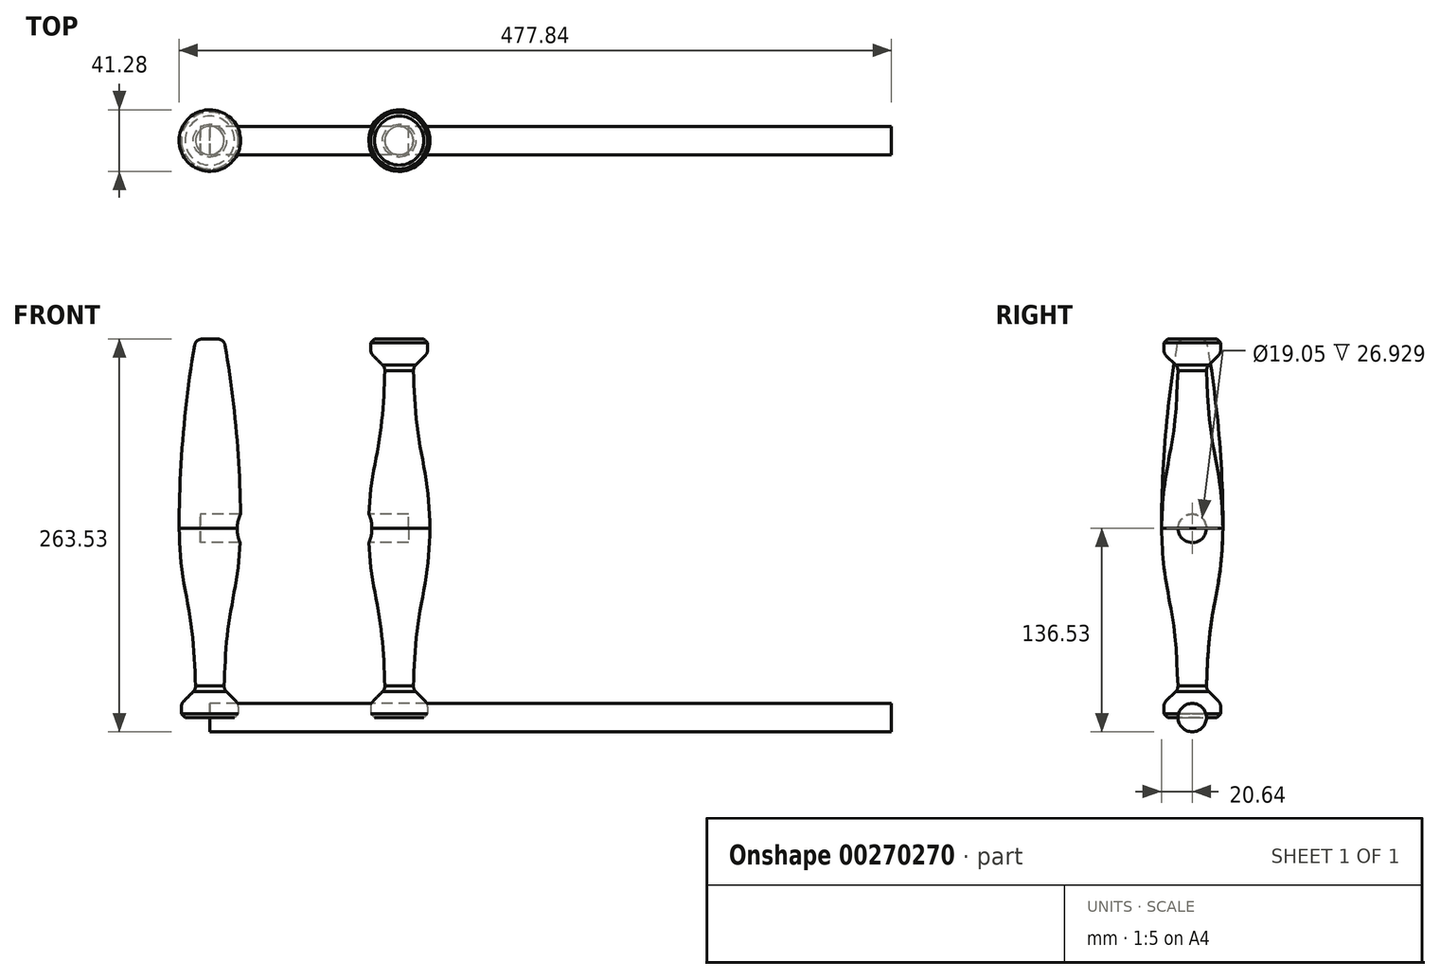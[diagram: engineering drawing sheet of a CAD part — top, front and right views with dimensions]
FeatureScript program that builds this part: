
annotation { "Feature Type Name" : "Feature", "Feature Type Description" : "" }
export const myFeature = defineFeature(function(context is Context, id is Id, definition is map)
    precondition{}
    {
        {
            var Q0;
            Q0=qCreatedBy(makeId("Top.planeOp"),FACE);
            var sketch = newSketch(context, id + "F0", { "sketchPlane" : qUnion([Q0])});
            skCircle(sketch, "E0", {"center": v(0, 0) * mm, "radius": 19.05 * mm});
            skSolve(sketch);
        }
        {
            var Q0;
            Q0=makeQuery(id+"F0.imprint","IMPRINT",FACE,{"disambiguationData":[TD([[makeQuery(id+"F0.imprint","IMPRINT",EDGE,{"derivedFrom":sQuery(id+"F0.wireOp",EDGE,"E0")}),1.0]])]});
            extrude(context, id + "F1", {"entities" : qUnion([Q0]), "depth" : 9.52 * mm});
        }
        {
            var Q0;
            Q0=qCreatedBy(makeId("Top.planeOp"),FACE);
            cPlane(context, id + "F2", {"entities" : qUnion([Q0]), "cplaneType" : CPlaneType.OFFSET, "offset" : 19.05 * mm, "width" : 152.4 * mm, "height" : 152.4 * mm});
        }
        {
            var Q0;
            Q0=qCreatedBy(id+"F2.planeOp",FACE);
            var sketch = newSketch(context, id + "F3", { "sketchPlane" : qUnion([Q0])});
            skCircle(sketch, "E1", {"center": v(0, 0) * mm, "radius": 9.53 * mm});
            skSolve(sketch);
        }
        {
            var Q0;
            Q0=qCreatedBy(makeId("Top.planeOp"),FACE);
            cPlane(context, id + "F4", {"entities" : qUnion([Q0]), "cplaneType" : CPlaneType.OFFSET, "offset" : 127 * mm, "width" : 152.4 * mm, "height" : 152.4 * mm});
        }
        {
            var Q0;
            Q0=qCreatedBy(id+"F4.planeOp",FACE);
            var sketch = newSketch(context, id + "F5", { "sketchPlane" : qUnion([Q0])});
            skCircle(sketch, "E2", {"center": v(0, 0) * mm, "radius": 20.64 * mm});
            skSolve(sketch);
        }
        {
            var Q0;
            Q0=qCreatedBy(makeId("Top.planeOp"),FACE);
            cPlane(context, id + "F6", {"entities" : qUnion([Q0]), "cplaneType" : CPlaneType.OFFSET, "offset" : 63.5 * mm, "width" : 152.4 * mm, "height" : 152.4 * mm});
        }
        {
            var Q0;
            Q0=qCreatedBy(id+"F6.planeOp",FACE);
            var sketch = newSketch(context, id + "F7", { "sketchPlane" : qUnion([Q0])});
            skCircle(sketch, "E3", {"center": v(0, 0) * mm, "radius": 12.7 * mm});
            skSolve(sketch);
        }
        {
            var Q0;
            Q0=qCreatedBy(makeId("Top.planeOp"),FACE);
            cPlane(context, id + "F8", {"entities" : qUnion([Q0]), "cplaneType" : CPlaneType.OFFSET, "offset" : 101.6 * mm, "width" : 152.4 * mm, "height" : 152.4 * mm});
        }
        {
            var Q0;
            Q0=qCreatedBy(id+"F8.planeOp",FACE);
            var sketch = newSketch(context, id + "F9", { "sketchPlane" : qUnion([Q0])});
            skCircle(sketch, "E4", {"center": v(0, 0) * mm, "radius": 19.05 * mm});
            skSolve(sketch);
        }
        {
            var Q1;
            Q1=makeQuery(id+"F1.opExtrude","CAP_FACE",FACE,{"disambiguationData":[OSD([sQuery(id+"F0.wireOp",EDGE,"E0")])],"isStart":false});
            var Q2;
            Q2=makeQuery(id+"F3.imprint","IMPRINT",FACE,{"disambiguationData":[TD([[makeQuery(id+"F3.imprint","IMPRINT",EDGE,{"derivedFrom":sQuery(id+"F3.wireOp",EDGE,"E1")}),1.0]])]});
            loft(context, id + "F10", {"operationType" : NewBodyOperationType.ADD, "sheetProfilesArray" : [{ "sheetProfileEntities" : qUnion([Q1]) }, { "sheetProfileEntities" : qUnion([Q2]) }]});
        }
        {
            var Q1;
            Q1=makeQuery(id+"F10.opLoft","CAP_FACE",FACE,{"disambiguationData":[OSD([makeQuery(id+"F3.imprint","IMPRINT",FACE,{"disambiguationData":[TD([[makeQuery(id+"F3.imprint","IMPRINT",EDGE,{"derivedFrom":sQuery(id+"F3.wireOp",EDGE,"E1")}),1.0]])]})])],"isStart":true});
            var Q2;
            Q2=makeQuery(id+"F7.imprint","IMPRINT",FACE,{"disambiguationData":[TD([[makeQuery(id+"F7.imprint","IMPRINT",EDGE,{"derivedFrom":sQuery(id+"F7.wireOp",EDGE,"E3")}),1.0]])]});
            var Q3;
            Q3=makeQuery(id+"F9.imprint","IMPRINT",FACE,{"disambiguationData":[TD([[makeQuery(id+"F9.imprint","IMPRINT",EDGE,{"derivedFrom":sQuery(id+"F9.wireOp",EDGE,"E4")}),1.0]])]});
            var Q4;
            Q4=makeQuery(id+"F5.imprint","IMPRINT",FACE,{"disambiguationData":[TD([[makeQuery(id+"F5.imprint","IMPRINT",EDGE,{"derivedFrom":sQuery(id+"F5.wireOp",EDGE,"E2")}),1.0]])]});
            loft(context, id + "F11", {"operationType" : NewBodyOperationType.ADD, "sheetProfilesArray" : [{ "sheetProfileEntities" : qUnion([Q1]) }, { "sheetProfileEntities" : qUnion([Q2]) }, { "sheetProfileEntities" : qUnion([Q3]) }, { "sheetProfileEntities" : qUnion([Q4]) }]});
        }
        {
            var Q0;
            Q0=makeQuery(id+"F1.opExtrude","CAP_EDGE",EDGE,{"disambiguationData":[OSD([sQuery(id+"F0.wireOp",EDGE,"E0")])],"isStart":true});
            chamfer(context, id + "F12", {"entities" : qUnion([Q0]), "width" : 2.54 * mm, "tangentPropagation" : true});
        }
        {
            var Q0;
            {var subQ0=sQuery(id+"F0.wireOp",EDGE,"E0");Q0=makeQuery(id+"F10.boolean.opBoolean","MERGE",EDGE,{"derivedFrom":[makeQuery(id+"F1.opExtrude","CAP_EDGE",EDGE,{"disambiguationData":[OSD([subQ0])],"isStart":false}),makeQuery(id+"F10.opLoft","MID_CAP_EDGE",EDGE,{"disambiguationData":[OSD([subQ0])],"capPos":0.0})]});}
            var Q1;
            {var subQ0=sQuery(id+"F3.wireOp",EDGE,"E1");var subQ1=sQuery(id+"F0.wireOp",EDGE,"E0");Q1=makeQuery(id+"F11.boolean.opBoolean","MERGE",EDGE,{"derivedFrom":[makeQuery(id+"F10.opLoft","MID_CAP_EDGE",EDGE,{"disambiguationData":[OSD([subQ1,subQ0])],"capPos":1.0}),makeQuery(id+"F11.opLoft","MID_CAP_EDGE",EDGE,{"disambiguationData":[OSD([subQ1,subQ0])],"capPos":0.0})]});}
            fillet(context, id + "F13", {"entities" : qUnion([Q0, Q1]), "radius" : 5.08 * mm, "tangentPropagation" : true, "allowEdgeOverflow" : false});
        }
        {
            var Q0;
            Q0=makeQuery(id+"F1.opExtrude","SWEPT_BODY",BODY,{"disambiguationData":[OSD([sQuery(id+"F0.wireOp",EDGE,"E0")])]});
            transform(context, id + "F14", {"entities" : qUnion([Q0]), "transformType" : TransformType.TRANSLATION_3D, "dx" : 127 * mm, "dy" : 0 * mm, "dz" : 0 * mm, "makeCopy" : true});
        }
        {
            var Q0;
            Q0=makeQuery(id+"F14.opPattern","COPY",BODY,{"derivedFrom":makeQuery(id+"F1.opExtrude","SWEPT_BODY",BODY,{"disambiguationData":[OSD([sQuery(id+"F0.wireOp",EDGE,"E0")])]}),"instanceName":"1"});
            var Q1;
            Q1=qCreatedBy(id+"F4.planeOp",FACE);
            mirror(context, id + "F15", {"operationType" : NewBodyOperationType.ADD, "entities" : qUnion([Q0]), "mirrorPlane" : qUnion([Q1])});
        }
        {
            var Q0;
            Q0=qCreatedBy(makeId("Front.planeOp"),FACE);
            var sketch = newSketch(context, id + "F16", { "sketchPlane" : qUnion([Q0])});
            skFitSpline(sketch, "E5.0", {"points": [v(20.64, 127) * mm, v(6.88, 127) * mm, v(-6.88, 127) * mm, v(-20.64, 127) * mm]});
            skLineSegment(sketch, "E6", {"start": v(0, 127) * mm, "end": v(0, 254) * mm});
            skLineSegment(sketch, "E7", {"start": v(0, 254) * mm, "end": v(9.52, 254) * mm});
            skArc(sketch, "E8", {"start": v(20.64, 127) * mm, "mid": v(17.85, 190.74) * mm, "end": v(9.53, 254) * mm});
            skLineSegment(sketch, "E9", {"start": v(20.64, 127) * mm, "end": v(20.64, 174.94) * mm, "construction": true});
            skSolve(sketch);
        }
        {
            var Q0;
            {var subQ2=sQuery(id+"F16.wireOp",EDGE,"E6");Q0=makeQuery(id+"F16.imprint","IMPRINT",FACE,{"disambiguationData":[TD([[makeQuery(id+"F16.imprint","IMPRINT",EDGE,{"derivedFrom":subQ2}),-1.0]])]});}
            var Q1;
            Q1=sQuery(id+"F16.wireOp",EDGE,"E6");
            revolve(context, id + "F17", {"operationType" : NewBodyOperationType.ADD, "entities" : qUnion([Q0]), "axis" : qUnion([Q1]), "revolveType" : RevolveType.FULL});
        }
        {
            var Q0;
            Q0=makeQuery(id+"F17.opRevolve","SWEPT_EDGE",EDGE,{"disambiguationData":[OSD([sQuery(id+"F16.wireOp",EDGE,"E7"),sQuery(id+"F16.wireOp",EDGE,"E8")])]});
            fillet(context, id + "F18", {"entities" : qUnion([Q0]), "radius" : 5.08 * mm, "tangentPropagation" : true, "allowEdgeOverflow" : false});
        }
        {
            var Q0;
            Q0=qCreatedBy(makeId("Right.planeOp"),FACE);
            var sketch = newSketch(context, id + "F19", { "sketchPlane" : qUnion([Q0])});
            skFitSpline(sketch, "E10.0", {"points": [v(20.64, 127) * mm, v(6.88, 127) * mm, v(-6.88, 127) * mm, v(-20.64, 127) * mm]});
            skCircle(sketch, "E11", {"center": v(0, 127) * mm, "radius": 9.53 * mm});
            skSolve(sketch);
        }
        {
            var Q0;
            Q0 = qSketchRegion(id + "F19", true);
            var Q1;
            Q1=makeQuery(id+"F17.opRevolve","SWEPT_FACE",FACE,{"disambiguationData":[OSD([sQuery(id+"F16.wireOp",EDGE,"E8")])]});
            extrude(context, id + "F20", {"entities" : qUnion([Q0]), "operationType" : NewBodyOperationType.REMOVE, "endBoundEntityFace" : qUnion([Q1]), "depth" : 133.35 * mm, "hasSecondDirection" : true, "secondDirectionOppositeDirection" : true, "secondDirectionDepth" : 6.35 * mm});
        }
        {
            var Q0;
            Q0=qCreatedBy(makeId("Right.planeOp"),FACE);
            var sketch = newSketch(context, id + "F21", { "sketchPlane" : qUnion([Q0])});
            skCircle(sketch, "E12", {"center": v(0, 0) * mm, "radius": 9.53 * mm});
            skSolve(sketch);
        }
        {
            var Q0;
            Q0=makeQuery(id+"F21.imprint","IMPRINT",FACE,{"disambiguationData":[TD([[makeQuery(id+"F21.imprint","IMPRINT",EDGE,{"derivedFrom":sQuery(id+"F21.wireOp",EDGE,"E12")}),1.0]])]});
            extrude(context, id + "F22", {"entities" : qUnion([Q0]), "depth" : 457.2 * mm});
        }
    });
